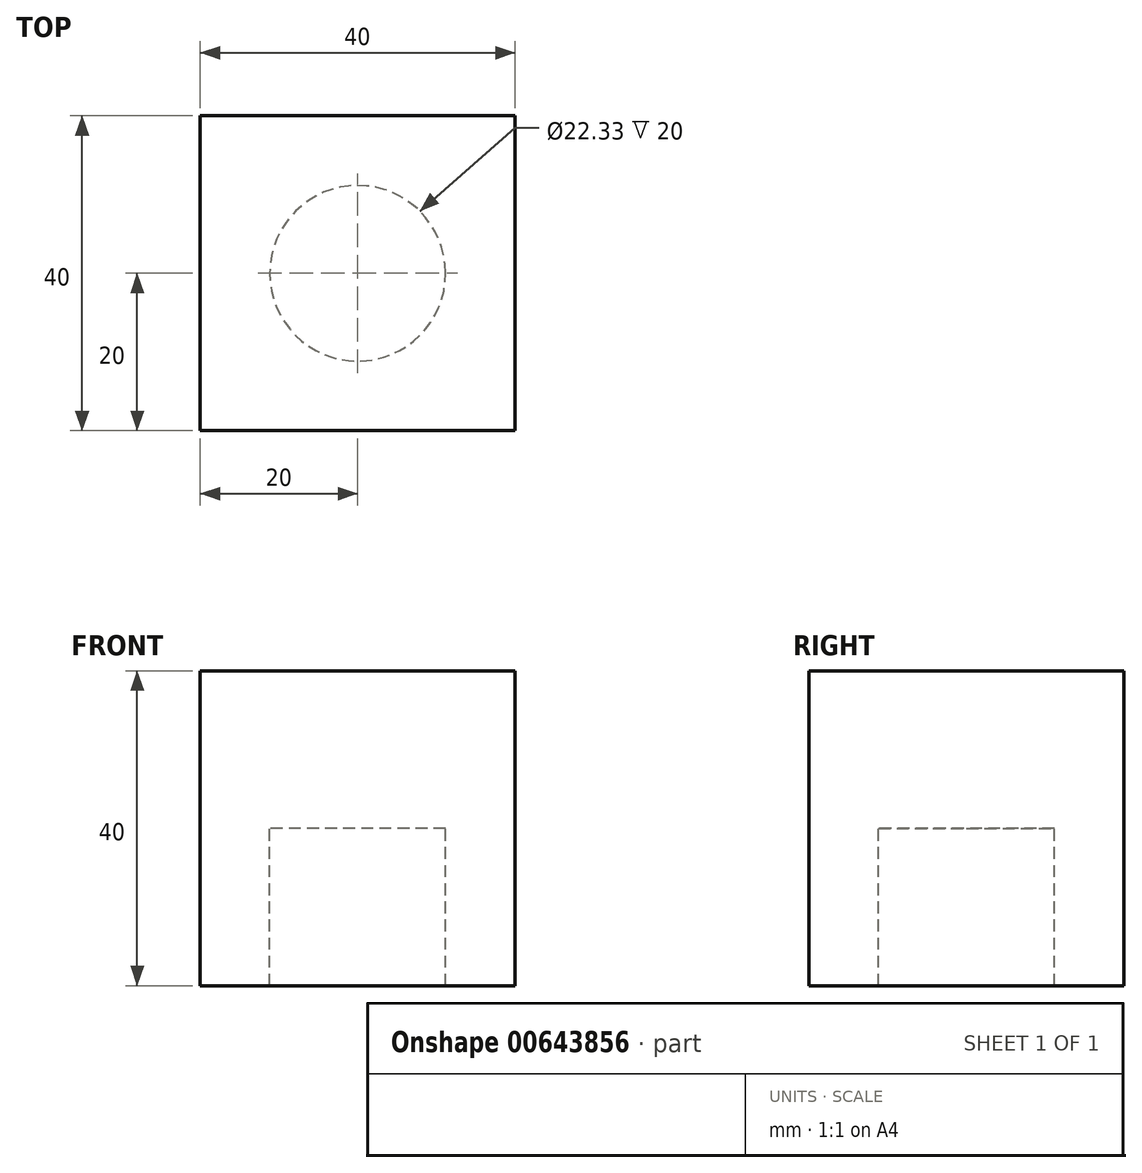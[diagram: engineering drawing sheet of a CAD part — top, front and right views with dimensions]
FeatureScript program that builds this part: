
annotation { "Feature Type Name" : "Feature", "Feature Type Description" : "" }
export const myFeature = defineFeature(function(context is Context, id is Id, definition is map)
    precondition{}
    {
        {
            var Q0;
            Q0=qCreatedBy(makeId("Top.planeOp"),FACE);
            var sketch = newSketch(context, id + "F0", { "sketchPlane" : qUnion([Q0])});
            skCircle(sketch, "E0.cCircle", {"center": v(0, 0) * mm, "radius": 20 * mm, "construction": true});
            skLineSegment(sketch, "E0.0", {"start": v(-20, 20) * mm, "end": v(20, 20) * mm});
            skLineSegment(sketch, "E0.1", {"start": v(20, 20) * mm, "end": v(20, -20) * mm});
            skLineSegment(sketch, "E0.2", {"start": v(20, -20) * mm, "end": v(-20, -20) * mm});
            skLineSegment(sketch, "E0.3", {"start": v(-20, -20) * mm, "end": v(-20, 20) * mm});
            skPoint(sketch, "E0.0.midPoint", {"position": v(0, 20) * mm});
            skSolve(sketch);
        }
        {
            var Q0;
            Q0=makeQuery(id+"F0.imprint","IMPRINT",FACE,{"disambiguationData":[TD([[makeQuery(id+"F0.imprint","IMPRINT",EDGE,{"derivedFrom":sQuery(id+"F0.wireOp",EDGE,"E0.0")}),-1.0]])]});
            extrude(context, id + "F1", {"entities" : qUnion([Q0]), "endBound" : BoundingType.SYMMETRIC, "depth" : 40 * mm, "offsetDistance" : 25.4 * mm});
        }
        {
            var Q0;
            Q0=sQuery(id+"F0.wireOp",VERTEX,"E0.cCircle.center");
            var Q1;
            Q1=makeQuery(id+"F1.opExtrude","SWEPT_BODY",BODY,{"disambiguationData":[OSD([sQuery(id+"F0.wireOp",EDGE,"E0.0"),sQuery(id+"F0.wireOp",EDGE,"E0.1"),sQuery(id+"F0.wireOp",EDGE,"E0.2"),sQuery(id+"F0.wireOp",EDGE,"E0.3")])]});
            hole(context, id + "F2", {"style" : HoleStyle.SIMPLE, "endStyle" : HoleEndStyle.THROUGH, "holeDiameter" : 22.33 * mm, "majorDiameter" : 6.35 * mm, "isTappedThrough" : true, "tappedDepth" : 12.7 * mm, "tapClearance" : 3, "locations" : qUnion([Q0]), "scope" : qUnion([Q1])});
        }
    });
